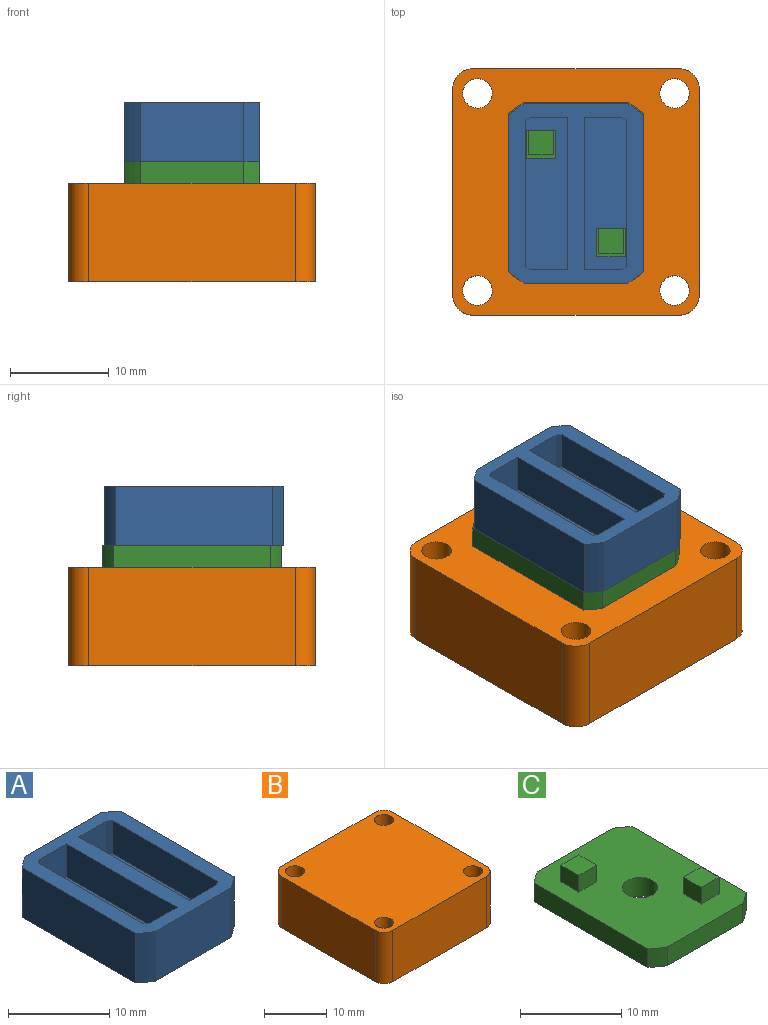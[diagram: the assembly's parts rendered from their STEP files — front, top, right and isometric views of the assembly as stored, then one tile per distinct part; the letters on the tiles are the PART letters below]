
ASSEMBLY  parts=3 mates=2
PART A: 32 faces, bbox 13.7x18.2x6 mm
  f0: plane 18.19x13.72mm, normal (0,0,-1), area 229.8mm2, adj f3,f4,f5,f6,f7,f8,f9,f22
  f1: plane 15.4x4.3mm, normal (0,0,1), area 57.9mm2, adj f15,f16,f17,f18,f19,f21,f28,f29
  f2: plane 15.4x4.3mm, normal (0,0,1), area 57.9mm2, adj f10,f11,f12,f13,f14,f20,f24,f25
  f3: plane 15.9x6mm, normal (1,0,0), area 95.4mm2, adj f0,f4,f22,f23
  f4: cylinder r=10.5mm len=6mm, axis (0,0,-1), area 11.9mm2, adj f0,f3,f5,f23
  f5: plane 10.5x6mm, normal (0,1,0), area 63mm2, adj f0,f4,f6,f23
  f6: cylinder r=10.5mm len=6mm, axis (0,0,-1), area 11.9mm2, adj f0,f5,f7,f23
  f7: plane 15.9x6mm, normal (-1,0,0), area 95.4mm2, adj f0,f6,f8,f23
  f8: cylinder r=10.5mm len=6mm, axis (0,0,-1), area 11.9mm2, adj f0,f7,f9,f23
  f9: plane 10.5x6mm, normal (0,-1,0), area 63mm2, adj f0,f8,f22,f23
  f10: cylinder r=9mm len=4mm, axis (0,0,-1), area 2.3mm2, adj f2,f11,f20,f23
  f11: plane 4x3.81mm, normal (0,-1,0), area 15.2mm2, adj f2,f10,f12,f23
  f12: plane 15.4x4mm, normal (-1,0,0), area 61.6mm2, adj f2,f11,f13,f23
  f13: plane 4x3.81mm, normal (0,1,0), area 15.2mm2, adj f2,f12,f14,f23
  f14: cylinder r=9mm len=4mm, axis (0,0,-1), area 2.3mm2, adj f2,f13,f20,f23
  f15: plane 4x3.81mm, normal (0,-1,0), area 15.2mm2, adj f1,f16,f21,f23
  f16: cylinder r=9mm len=4mm, axis (0,0,-1), area 2.3mm2, adj f1,f15,f17,f23
  f17: plane 14.76x4mm, normal (-1,0,0), area 59mm2, adj f1,f16,f18,f23
  f18: cylinder r=9mm len=4mm, axis (0,0,-1), area 2.3mm2, adj f1,f17,f19,f23
  f19: plane 4x3.81mm, normal (0,1,0), area 15.2mm2, adj f1,f18,f21,f23
  f20: plane 14.76x4mm, normal (1,0,0), area 59mm2, adj f2,f10,f14,f23
  f21: plane 15.4x4mm, normal (1,0,0), area 61.6mm2, adj f1,f15,f19,f23
  f22: cylinder r=10.5mm len=6mm, axis (0,0,-1), area 11.9mm2, adj f0,f3,f9,f23
  f23: plane 18.19x13.72mm, normal (0,0,1), area 113.9mm2, adj f3,f4,f5,f6,f7,f8,f9,f10
  f24: plane 2.85x2mm, normal (0,-1,0), area 5.7mm2, adj f0,f2,f25,f27
  f25: plane 2.85x2mm, normal (-1,0,0), area 5.7mm2, adj f0,f2,f24,f26
  f26: plane 2.85x2mm, normal (0,1,0), area 5.7mm2, adj f0,f2,f25,f27
  f27: plane 2.85x2mm, normal (1,0,0), area 5.7mm2, adj f0,f2,f24,f26
  f28: plane 2.85x2mm, normal (0,-1,0), area 5.7mm2, adj f0,f1,f29,f31
  f29: plane 2.85x2mm, normal (-1,0,0), area 5.7mm2, adj f0,f1,f28,f30
  f30: plane 2.85x2mm, normal (0,1,0), area 5.7mm2, adj f0,f1,f29,f31
  f31: plane 2.85x2mm, normal (1,0,0), area 5.7mm2, adj f0,f1,f28,f30
PART B: 14 faces, bbox 25x25x10 mm
  f0: plane 21x10mm, normal (0,1,0), area 210mm2, adj f8,f9,f10,f13
  f1: plane 21x10mm, normal (-1,0,0), area 210mm2, adj f8,f9,f10,f11
  f2: plane 21x10mm, normal (0,-1,0), area 210mm2, adj f8,f9,f11,f12
  f3: cylinder r=1.5mm len=10mm, axis (0,0,-1), area 94.2mm2, adj f8,f9
  f4: cylinder r=1.5mm len=10mm, axis (0,0,-1), area 94.2mm2, adj f8,f9
  f5: cylinder r=1.5mm len=10mm, axis (0,0,-1), area 94.2mm2, adj f8,f9
  f6: cylinder r=1.5mm len=10mm, axis (0,0,-1), area 94.2mm2, adj f8,f9
  f7: plane 21x10mm, normal (1,0,0), area 210mm2, adj f8,f9,f12,f13
  f8: plane 25x25mm, normal (0,0,1), area 593.3mm2, adj f0,f1,f2,f3,f4,f5,f6,f7
  f9: plane 25x25mm, normal (0,0,-1), area 593.3mm2, adj f0,f1,f2,f3,f4,f5,f6,f7
  f10: cylinder r=2mm len=10mm, axis (0,0,1), area 31.4mm2, adj f0,f1,f8,f9
  f11: cylinder r=2mm len=10mm, axis (0,0,-1), area 31.4mm2, adj f1,f2,f8,f9
  f12: cylinder r=2mm len=10mm, axis (0,0,1), area 31.4mm2, adj f2,f7,f8,f9
  f13: cylinder r=2mm len=10mm, axis (0,0,-1), area 31.4mm2, adj f0,f7,f8,f9
PART C: 21 faces, bbox 13.7x18.2x4.3 mm
  f0: plane 18.19x13.72mm, normal (0,0,1), area 223.9mm2, adj f1,f2,f3,f4,f5,f6,f7,f8
  f1: cylinder r=10.5mm len=2.25mm, axis (0,0,-1), area 4.4mm2, adj f0,f2,f8,f9
  f2: plane 15.9x2.25mm, normal (1,0,0), area 35.8mm2, adj f0,f1,f3,f9
  f3: cylinder r=10.5mm len=2.25mm, axis (0,0,-1), area 4.4mm2, adj f0,f2,f4,f9
  f4: plane 10.5x2.25mm, normal (0,1,0), area 23.6mm2, adj f0,f3,f5,f9
  f5: cylinder r=10.5mm len=2.25mm, axis (0,0,-1), area 4.4mm2, adj f0,f4,f6,f9
  f6: plane 15.9x2.25mm, normal (-1,0,0), area 35.8mm2, adj f0,f5,f7,f9
  f7: cylinder r=10.5mm len=2.25mm, axis (0,0,-1), area 4.4mm2, adj f0,f6,f8,f9
  f8: plane 10.5x2.25mm, normal (0,-1,0), area 23.6mm2, adj f0,f1,f7,f9
  f9: plane 18.19x13.72mm, normal (0,0,-1), area 236.4mm2, adj f1,f2,f3,f4,f5,f6,f7,f8
  f10: cylinder r=1.75mm len=3.5mm, axis (0,0,1), area 24.7mm2, adj f0,f9
  f11: plane 2.5x2mm, normal (0,-1,0), area 5mm2, adj f0,f12,f14,f15
  f12: plane 2.5x2mm, normal (1,0,0), area 5mm2, adj f0,f11,f13,f15
  f13: plane 2.5x2mm, normal (0,1,0), area 5mm2, adj f0,f12,f14,f15
  f14: plane 2.5x2mm, normal (-1,0,0), area 5mm2, adj f0,f11,f13,f15
  f15: plane 2.5x2.5mm, normal (0,0,1), area 6.2mm2, adj f11,f12,f13,f14
  f16: plane 2.5x2mm, normal (0,1,0), area 5mm2, adj f0,f17,f19,f20
  f17: plane 2.5x2mm, normal (-1,0,0), area 5mm2, adj f0,f16,f18,f20
  f18: plane 2.5x2mm, normal (0,-1,0), area 5mm2, adj f0,f17,f19,f20
  f19: plane 2.5x2mm, normal (1,0,0), area 5mm2, adj f0,f16,f18,f20
  f20: plane 2.5x2.5mm, normal (0,0,1), area 6.2mm2, adj f16,f17,f18,f19
PLACE A t=(-30.37,-11.17,-8.92)mm
PLACE B t=(-0.37,-10.99,-21.17)mm
PLACE C t=(29.63,-10.99,-11.17)mm
MATE fastened C.f3 <-> B.f8  axis (0,0,-1) through (-0.37,-10.99,-11.17)mm
MATE fastened C.f15 <-> A.f2  axis (0,0,1) through (-3.92,-4.74,-6.92)mm
